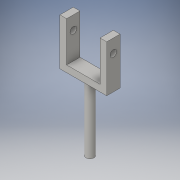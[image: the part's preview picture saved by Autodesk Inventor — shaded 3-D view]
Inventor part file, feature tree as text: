
AUTODESK INVENTOR PART (.ipt)
format: ipt  version: 2016 (Build 200138000, 138)  size: 116,736 bytes
history: native  units: in
note: dims shown in document units (in); Inventor stores cm internally (conversion verified against a paired STEP export)
features: extrude x3, sketch x3
ambient origin geometry x8: Origin, YZ Plane, XZ Plane, XY Plane, X Axis, Y Axis, Z Axis, Center Point
bodies: Solid1 (feature_tree)
feature tree (6):
  extrude  "Extrusion1"  Depth=1.1811in
  extrude  "Extrusion2"  Depth=1.378in
  extrude  "Extrusion3"  Depth=1.378in
  sketch  "Sketch1"  dims[d0=0.4921in d1=1.1811in]
  sketch  "Sketch2"  dims[d2=0.1969in d3=1.378in]
  sketch  "Sketch3"  dims[d4=1.378in d5=1.378in d6=0.1969in d8=1.1811in d9=0.3937in d10=0.0in d11=0.2362in d12=1.9685in d13=0.0in d14=0.3937in d15=0.1969in d16=1.378in d17=0.0in]
